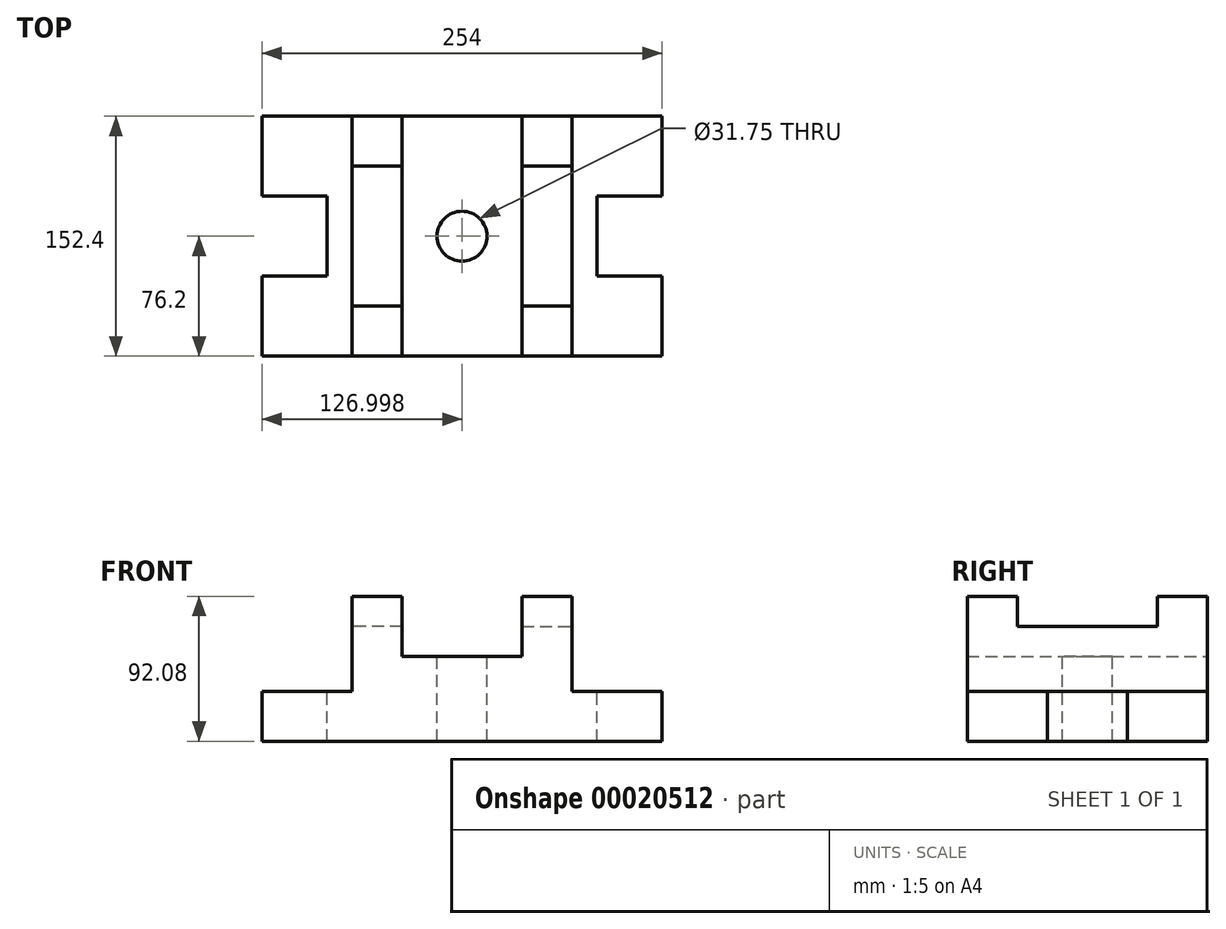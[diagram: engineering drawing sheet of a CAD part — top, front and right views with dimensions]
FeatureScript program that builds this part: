
annotation { "Feature Type Name" : "Feature", "Feature Type Description" : "" }
export const myFeature = defineFeature(function(context is Context, id is Id, definition is map)
    precondition{}
    {
        {
            var Q0;
            Q0=qCreatedBy(makeId("Front.planeOp"),FACE);
            var sketch = newSketch(context, id + "F0", { "sketchPlane" : qUnion([Q0])});
            skLineSegment(sketch, "E0", {"start": v(-64.6, -16.69) * mm, "end": v(62.4, -16.69) * mm});
            skLineSegment(sketch, "E1", {"start": v(-64.6, -16.69) * mm, "end": v(-64.6, 37.29) * mm});
            skLineSegment(sketch, "E2", {"start": v(-64.6, 37.29) * mm, "end": v(-26.5, 37.29) * mm});
            skLineSegment(sketch, "E3", {"start": v(62.4, -16.69) * mm, "end": v(62.4, 15.06) * mm});
            skLineSegment(sketch, "E4", {"start": v(-26.5, 37.29) * mm, "end": v(-26.5, 75.39) * mm});
            skLineSegment(sketch, "E5", {"start": v(-26.5, 75.39) * mm, "end": v(5.26, 75.39) * mm});
            skLineSegment(sketch, "E6", {"start": v(5.26, 75.39) * mm, "end": v(5.26, 15.06) * mm});
            skLineSegment(sketch, "E7", {"start": v(5.26, 15.06) * mm, "end": v(62.4, 15.06) * mm});
            skSolve(sketch);
        }
        {
            var Q0;
            Q0=makeQuery(id+"F0.imprint","IMPRINT",FACE,{"disambiguationData":[TD([[makeQuery(id+"F0.imprint","IMPRINT",EDGE,{"derivedFrom":sQuery(id+"F0.wireOp",EDGE,"E0")}),1.0]])]});
            extrude(context, id + "F1", {"entities" : qUnion([Q0]), "depth" : 76.2 * mm});
        }
        {
            var Q0;
            Q0=makeQuery(id+"F1.opExtrude","SWEPT_FACE",FACE,{"disambiguationData":[OSD([sQuery(id+"F0.wireOp",EDGE,"E6")])]});
            var sketch = newSketch(context, id + "F2", { "sketchPlane" : qUnion([Q0])});
            skLineSegment(sketch, "E8", {"start": v(-76.2, 75.39) * mm, "end": v(-44.45, 75.39) * mm});
            skLineSegment(sketch, "E9", {"start": v(-44.45, 75.39) * mm, "end": v(-44.45, 56.34) * mm});
            skLineSegment(sketch, "E10", {"start": v(-44.45, 56.34) * mm, "end": v(0, 56.34) * mm});
            skSolve(sketch);
        }
        {
            var Q0;
            {var subQ2=sQuery(id+"F2.wireOp",EDGE,"E9");Q0=makeQuery(id+"F2.imprint","IMPRINT",FACE,{"disambiguationData":[TD([[makeQuery(id+"F2.imprint","IMPRINT",EDGE,{"derivedFrom":subQ2}),1.0]])]});}
            var Q1;
            Q1 = qSketchRegion(id + "F4", true);
            extrude(context, id + "F3", {"entities" : qUnion([Q0, Q1]), "operationType" : NewBodyOperationType.REMOVE, "endBound" : BoundingType.THROUGH_ALL, "oppositeDirection" : true, "depth" : 33.83 * mm});
        }
        {
            var Q0;
            Q0=makeQuery(id+"F1.opExtrude","SWEPT_FACE",FACE,{"disambiguationData":[OSD([sQuery(id+"F0.wireOp",EDGE,"E7")])]});
            var sketch = newSketch(context, id + "F4", { "sketchPlane" : qUnion([Q0])});
            skLineSegment(sketch, "E11", {"start": v(62.4, -76.2) * mm, "end": v(62.4, -25.4) * mm});
            skLineSegment(sketch, "E12", {"start": v(62.4, -25.4) * mm, "end": v(21.13, -25.4) * mm});
            skLineSegment(sketch, "E13", {"start": v(21.13, -25.4) * mm, "end": v(21.13, 0) * mm});
            skSolve(sketch);
        }
        {
            var Q0;
            {var subQ5=sQuery(id+"F4.wireOp",EDGE,"E12");Q0=makeQuery(id+"F4.imprint","IMPRINT",FACE,{"disambiguationData":[TD([[makeQuery(id+"F4.imprint","IMPRINT",EDGE,{"derivedFrom":subQ5}),-1.0]])]});}
            extrude(context, id + "F5", {"entities" : qUnion([Q0]), "operationType" : NewBodyOperationType.REMOVE, "endBound" : BoundingType.THROUGH_ALL, "oppositeDirection" : true, "depth" : 25.4 * mm});
        }
        {
            var Q0;
            Q0=makeQuery(id+"F1.opExtrude","SWEPT_BODY",BODY,{"disambiguationData":[OSD([sQuery(id+"F0.wireOp",EDGE,"E0"),sQuery(id+"F0.wireOp",EDGE,"E1"),sQuery(id+"F0.wireOp",EDGE,"E2"),sQuery(id+"F0.wireOp",EDGE,"E3"),sQuery(id+"F0.wireOp",EDGE,"E4"),sQuery(id+"F0.wireOp",EDGE,"E5"),sQuery(id+"F0.wireOp",EDGE,"E6"),sQuery(id+"F0.wireOp",EDGE,"E7")])]});
            var Q1;
            Q1=makeQuery(id+"F1.opExtrude","CAP_FACE",FACE,{"disambiguationData":[OSD([sQuery(id+"F0.wireOp",EDGE,"E0"),sQuery(id+"F0.wireOp",EDGE,"E1"),sQuery(id+"F0.wireOp",EDGE,"E2"),sQuery(id+"F0.wireOp",EDGE,"E3"),sQuery(id+"F0.wireOp",EDGE,"E4"),sQuery(id+"F0.wireOp",EDGE,"E5"),sQuery(id+"F0.wireOp",EDGE,"E6"),sQuery(id+"F0.wireOp",EDGE,"E7")])],"isStart":true});
            mirror(context, id + "F6", {"operationType" : NewBodyOperationType.ADD, "entities" : qUnion([Q0]), "mirrorPlane" : qUnion([Q1])});
        }
        {
            var Q0;
            Q0=makeQuery(id+"F1.opExtrude","SWEPT_BODY",BODY,{"disambiguationData":[OSD([sQuery(id+"F0.wireOp",EDGE,"E0"),sQuery(id+"F0.wireOp",EDGE,"E1"),sQuery(id+"F0.wireOp",EDGE,"E2"),sQuery(id+"F0.wireOp",EDGE,"E3"),sQuery(id+"F0.wireOp",EDGE,"E4"),sQuery(id+"F0.wireOp",EDGE,"E5"),sQuery(id+"F0.wireOp",EDGE,"E6"),sQuery(id+"F0.wireOp",EDGE,"E7")])]});
            var Q1;
            {var subQ0=makeQuery(id+"F1.opExtrude","SWEPT_FACE",FACE,{"disambiguationData":[OSD([sQuery(id+"F0.wireOp",EDGE,"E1")])]});Q1=makeQuery(id+"F6.boolean.opBoolean","MERGE",FACE,{"derivedFrom":[subQ0,makeQuery(id+"F6.opPattern","COPY",FACE,{"derivedFrom":subQ0,"instanceName":"1"})]});}
            mirror(context, id + "F7", {"operationType" : NewBodyOperationType.ADD, "entities" : qUnion([Q0]), "mirrorPlane" : qUnion([Q1])});
        }
        {
            var Q0;
            {var subQ0=makeQuery(id+"F1.opExtrude","SWEPT_FACE",FACE,{"disambiguationData":[OSD([sQuery(id+"F0.wireOp",EDGE,"E2")])]});var subQ1=makeQuery(id+"F6.boolean.opBoolean","MERGE",FACE,{"derivedFrom":[subQ0,makeQuery(id+"F6.opPattern","COPY",FACE,{"derivedFrom":subQ0,"instanceName":"1"})]});Q0=makeQuery(id+"F7.boolean.opBoolean","MERGE",FACE,{"derivedFrom":[subQ1,makeQuery(id+"F7.opPattern","COPY",FACE,{"derivedFrom":subQ1,"instanceName":"1"})]});}
            var sketch = newSketch(context, id + "F8", { "sketchPlane" : qUnion([Q0])});
            skCircle(sketch, "E14", {"center": v(-64.6, 0) * mm, "radius": 15.88 * mm});
            skPoint(sketch, "E15.orphan", {"position": v(-64.6, -76.2) * mm});
            skSolve(sketch);
        }
        {
            var Q0;
            Q0=makeQuery(id+"F8.imprint","IMPRINT",FACE,{"disambiguationData":[TD([[makeQuery(id+"F8.imprint","IMPRINT",EDGE,{"derivedFrom":sQuery(id+"F8.wireOp",EDGE,"E14")}),1.0]])]});
            extrude(context, id + "F9", {"entities" : qUnion([Q0]), "operationType" : NewBodyOperationType.REMOVE, "endBound" : BoundingType.THROUGH_ALL, "oppositeDirection" : true, "depth" : 25.4 * mm});
        }
    });
